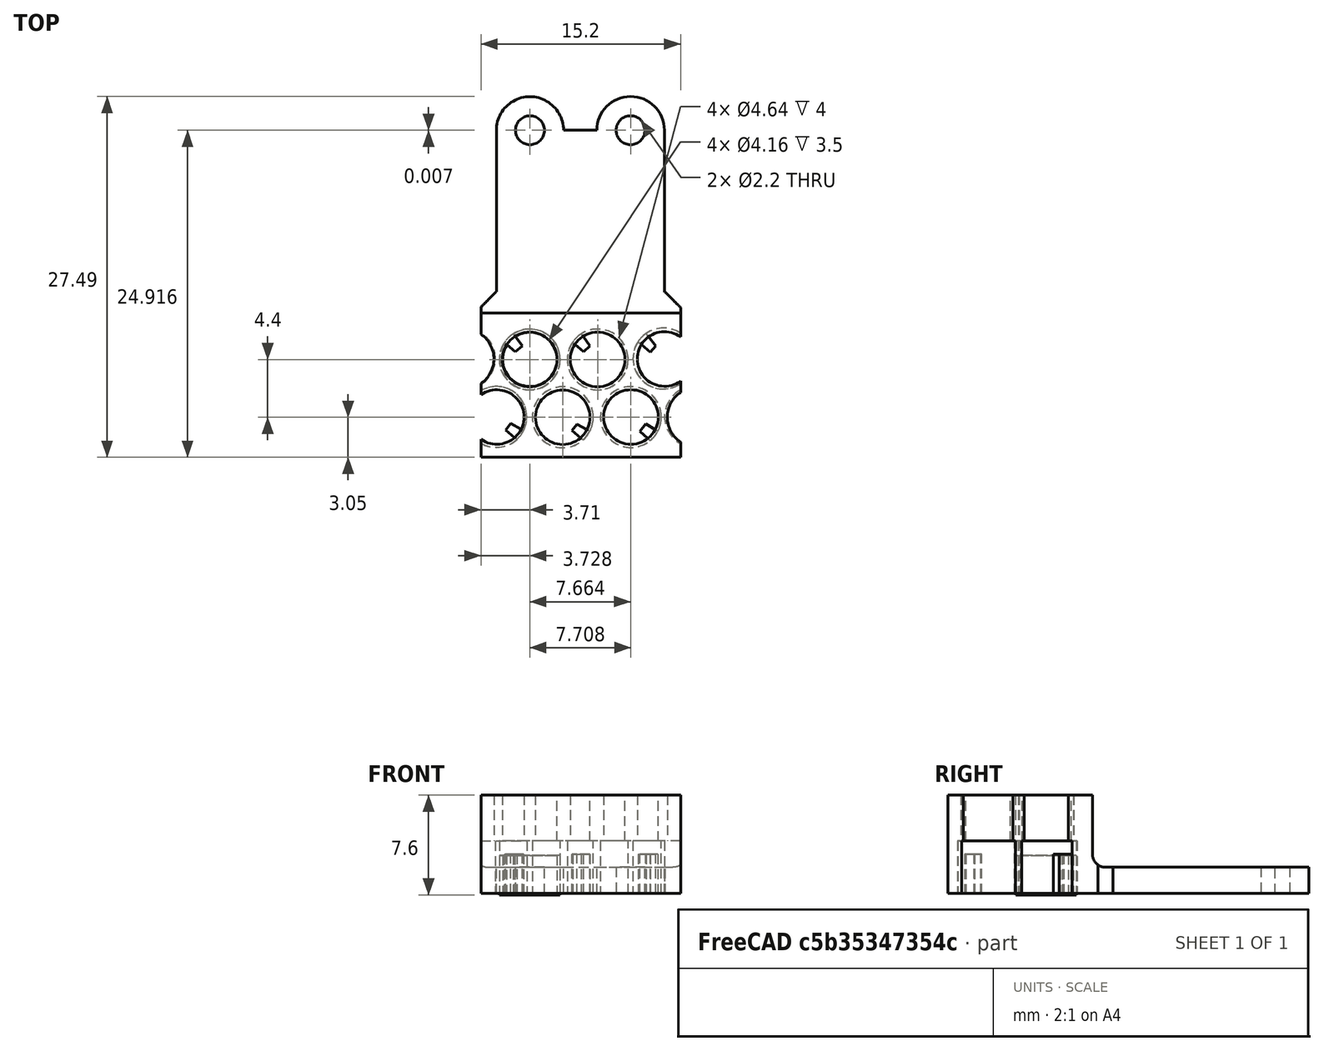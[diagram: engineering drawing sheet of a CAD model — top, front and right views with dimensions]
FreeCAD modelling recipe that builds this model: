
FCSTD DOCUMENT  (FreeCAD 0.16R6706 (Git))
Label: MotorHolder_1.1
License: All rights reserved
LicenseURL: http://en.wikipedia.org/wiki/All_rights_reserved
objects: Sketcher::SketchObject×4, PartDesign::Pad×4, Part::MultiFuse×2, Mesh::Feature×1, Part::Feature×1, PartDesign::Chamfer×1, Part::Box×1, Part::Cut×1, PartDesign::Fillet×1
note: 19 computed .brp shape members not serialized (recipe doc carries the construction recipe); baked Part::Feature solids carry a one-line shape summary decoded from their .brp

FEATURE [Mesh::Feature] Motor_Holder_2_1  label="Motor Holder 2.1"
FEATURE [Sketcher::SketchObject] Sketch
  Placement = pos=(0,0,-0.1) rot=(0,0,1;0rad)
  sketch-geometry (4):
    g0: LineSegment StartX=2.61412 StartY=9.20943 StartZ=0 EndX=2.48015 EndY=9.39721 EndZ=0
    g1: LineSegment StartX=1.96858 StartY=8.56337 StartZ=0 EndX=1.796 EndY=8.72024 EndZ=0
    g2: ArcOfCircle CenterX=3.71702 CenterY=7.46188 CenterZ=0 NormalX=0 NormalY=0 NormalZ=1 Radius=2.06647 StartAngle=2.57941 EndAngle=8.41696
    g3: ArcOfCircle CenterX=3.72 CenterY=7.46 CenterZ=0 NormalX=0 NormalY=0 NormalZ=1 Radius=2.3 StartAngle=2.5617 EndAngle=8.42331
  constraints (4):
    c: Coincident(g2,g0)
    c: Coincident(g2,g1)
    c: Coincident(g3,g0)
    c: Coincident(g3,g1)
FEATURE [Part::Feature] Solid
  shape: bbox 15.36 x 27.48 x 8.96 mm, 598 faces (baked)
FEATURE [PartDesign::Pad] Pad
  Length = 3
  Length2 = 100
  Placement = pos=(0,0,-0.1) rot=(0,0,1;0rad)
  Sketch = -> Sketch
  Type = 0
FEATURE [Sketcher::SketchObject] Sketch001
  sketch-geometry (24):
    g0: LineSegment StartX=1.16719 StartY=12.6074 StartZ=0 EndX=1.16719 EndY=24.9153 EndZ=0
    g1: LineSegment StartX=6.28798 StartY=24.9169 StartZ=0 EndX=8.82572 EndY=24.9169 EndZ=0
    g2: LineSegment StartX=13.9682 StartY=12.5724 StartZ=0 EndX=13.9682 EndY=24.9342 EndZ=0
    g3: ArcOfCircle CenterX=3.72758 CenterY=24.9165 CenterZ=0 NormalX=0 NormalY=0 NormalZ=1 Radius=2.56039 StartAngle=0.000160774 EndAngle=3.14208
    g4: ArcOfCircle CenterX=11.397 CenterY=24.9235 CenterZ=0 NormalX=0 NormalY=0 NormalZ=1 Radius=2.57125 StartAngle=0.00415218 EndAngle=3.14415
    g5: Circle CenterX=3.72758 CenterY=24.9165 CenterZ=0 NormalX=0 NormalY=0 NormalZ=1 Radius=1.1
    g6: Circle CenterX=11.392 CenterY=24.9235 CenterZ=0 NormalX=0 NormalY=0 NormalZ=1 Radius=1.1
    g7: LineSegment StartX=0 StartY=0 StartZ=0 EndX=15.2 EndY=0 EndZ=0
    g8: LineSegment StartX=15.2 StartY=12.5724 StartZ=0 EndX=13.9682 EndY=12.5724 EndZ=0
    g9: LineSegment StartX=0 StartY=12.6074 StartZ=0 EndX=1.16719 EndY=12.6074 EndZ=0
    g10: Circle CenterX=3.71 CenterY=7.45 CenterZ=0 NormalX=0 NormalY=0 NormalZ=1 Radius=2.32
    g11: Circle CenterX=8.8865 CenterY=7.45 CenterZ=0 NormalX=0 NormalY=0 NormalZ=1 Radius=2.32
    g12: Circle CenterX=11.4178 CenterY=3.06406 CenterZ=0 NormalX=0 NormalY=0 NormalZ=1 Radius=2.32
    g13: Circle CenterX=6.22788 CenterY=3.05007 CenterZ=0 NormalX=0 NormalY=0 NormalZ=1 Radius=2.32
    g14: ArcOfCircle CenterX=-1.2323 CenterY=7.51766 CenterZ=0 NormalX=0 NormalY=0 NormalZ=1 Radius=2.32 StartAngle=5.27236 EndAngle=7.29401
    g15: ArcOfCircle CenterX=1.16612 CenterY=3.07188 CenterZ=0 NormalX=0 NormalY=0 NormalZ=1 Radius=2.32 StartAngle=4.18574 EndAngle=8.38063
    g16: ArcOfCircle CenterX=13.8979 CenterY=7.52681 CenterZ=0 NormalX=0 NormalY=0 NormalZ=1 Radius=2.32 StartAngle=0.974907 EndAngle=5.30828
    g17: LineSegment StartX=15.2 StartY=9.44695 StartZ=0 EndX=15.2 EndY=12.5724 EndZ=0
    g18: LineSegment StartX=15.2 StartY=5.60666 StartZ=0 EndX=15.2 EndY=5.12562 EndZ=0
    g19: LineSegment StartX=15.2 StartY=1.04863 StartZ=0 EndX=15.2 EndY=0 EndZ=0
    g20: LineSegment StartX=0 StartY=0 StartZ=0 EndX=0 EndY=1.06625 EndZ=0
    g21: LineSegment StartX=0 StartY=5.07751 StartZ=0 EndX=0 EndY=5.55199 EndZ=0
    g22: LineSegment StartX=0 StartY=9.48333 StartZ=0 EndX=0 EndY=12.6074 EndZ=0
    g23: ArcOfCircle CenterX=16.3077 CenterY=3.08713 CenterZ=0 NormalX=0 NormalY=0 NormalZ=1 Radius=2.32 StartAngle=2.06854 EndAngle=4.21464
  constraints (50):
    c: Vertical(g0)
    c: Horizontal(g1)
    c: Vertical(g2)
    c: Coincident(g3,g0)
    c: Coincident(g3,g1)
    c: Coincident(g4,g1)
    c: Coincident(g4,g2)
    c: Coincident(g5,g3)
    c: Horizontal(g7)
    c: Coincident(g7,g-1)
    c: Coincident(g8,g2)
    c: Horizontal(g8)
    c: Coincident(g9,g0)
    c: Horizontal(g9)
    c: Radius(g10) = 2.32
    c: DistanceY(g-1,g10) = 7.45
    c: DistanceX(g-1,g10) = 3.71
    c: Radius(g11) = 2.32
    c: Radius(g12) = 2.32
    c: Radius(g13) = 2.32
    c: Radius(g15) = 2.32
    c: Radius(g16) = 2.32
    c: DistanceY(g-1,g11) = 7.45
    c: Coincident(g17,g16)
    c: Coincident(g17,g8)
    c: Vertical(g17)
    c: Coincident(g18,g16)
    c: Vertical(g18)
    c: Coincident(g19,g7)
    c: Vertical(g19)
    c: Coincident(g20,g-1)
    c: Coincident(g20,g15)
    c: Vertical(g20)
    c: Coincident(g21,g15)
    c: Coincident(g21,g14)
    c: Vertical(g21)
    c: Coincident(g22,g14)
    c: Coincident(g22,g9)
    c: Vertical(g22)
    c: DistanceX(g9,g8) = 15.2
    c: DistanceX(g14,g16) = 15.2
    c: DistanceX(g-1,g7) = 15.2
    c: Coincident(g23,g18)
    c: Coincident(g23,g19)
    c: DistanceX(g-1,g14) = 0
    c: DistanceX(g-1,g15) = 0
    c: Radius(g14) = 2.32
    c: Radius(g23) = 2.32
    c: Radius(g5) = 1.1
    c: Radius(g6) = 1.1
FEATURE [PartDesign::Pad] Pad001
  Length = 4
  Length2 = 100
  Sketch = -> Sketch001
  Type = 0
FEATURE [Sketcher::SketchObject] Sketch002
  Placement = pos=(0,0,4) rot=(0,0,1;0rad)
  sketch-geometry (16):
    g0: LineSegment StartX=0 StartY=0 StartZ=0 EndX=15.2 EndY=0 EndZ=0
    g1: Circle CenterX=3.71 CenterY=7.45 CenterZ=0 NormalX=0 NormalY=0 NormalZ=1 Radius=2.08
    g2: Circle CenterX=8.8865 CenterY=7.45 CenterZ=0 NormalX=0 NormalY=0 NormalZ=1 Radius=2.08
    g3: Circle CenterX=11.4178 CenterY=3.06406 CenterZ=0 NormalX=0 NormalY=0 NormalZ=1 Radius=2.08
    g4: Circle CenterX=6.22788 CenterY=3.05007 CenterZ=0 NormalX=0 NormalY=0 NormalZ=1 Radius=2.08
    g5: ArcOfCircle CenterX=-1.29213 CenterY=7.49891 CenterZ=0 NormalX=0 NormalY=0 NormalZ=1 Radius=2.27568 StartAngle=5.31622 EndAngle=7.25015
    g6: ArcOfCircle CenterX=1.20105 CenterY=3.06417 CenterZ=0 NormalX=0 NormalY=0 NormalZ=1 Radius=2.08 StartAngle=4.09681 EndAngle=8.46956
    g7: ArcOfCircle CenterX=13.9805 CenterY=7.48824 CenterZ=0 NormalX=0 NormalY=0 NormalZ=1 Radius=2.08 StartAngle=0.944332 EndAngle=5.33885
    g8: LineSegment StartX=15.2 StartY=5.80322 StartZ=0 EndX=15.2 EndY=4.94257 EndZ=0
    g9: LineSegment StartX=15.2 StartY=1.15374 StartZ=0 EndX=15.2 EndY=0 EndZ=0
    g10: LineSegment StartX=0 StartY=0 StartZ=0 EndX=0 EndY=1.36598 EndZ=0
    g11: LineSegment StartX=0 StartY=4.76237 StartZ=0 EndX=0 EndY=5.62564 EndZ=0
    g12: ArcOfCircle CenterX=16.4748 CenterY=3.04816 CenterZ=0 NormalX=0 NormalY=0 NormalZ=1 Radius=2.28338 StartAngle=2.1631 EndAngle=4.12008
    g13: LineSegment StartX=0 StartY=11 StartZ=0 EndX=15.2 EndY=11 EndZ=0
    g14: LineSegment StartX=15.2 StartY=9.17326 StartZ=0 EndX=15.2 EndY=11 EndZ=0
    g15: LineSegment StartX=0 StartY=9.37218 StartZ=0 EndX=0 EndY=11 EndZ=0
  constraints (36):
    c: Horizontal(g0)
    c: Coincident(g0,g-1)
    c: Radius(g1) = 2.08
    c: DistanceY(g-1,g1) = 7.45
    c: DistanceX(g-1,g1) = 3.71
    c: Radius(g2) = 2.08
    c: Radius(g3) = 2.08
    c: Radius(g4) = 2.08
    c: Radius(g6) = 2.08
    c: Radius(g7) = 2.08
    c: DistanceY(g-1,g2) = 7.45
    c: Coincident(g8,g7)
    c: Vertical(g8)
    c: Coincident(g9,g0)
    c: Vertical(g9)
    c: Coincident(g10,g-1)
    c: Coincident(g10,g6)
    c: Vertical(g10)
    c: Coincident(g11,g6)
    c: Coincident(g11,g5)
    c: Vertical(g11)
    c: DistanceX(g5,g7) = 15.2
    c: DistanceX(g-1,g0) = 15.2
    c: Coincident(g12,g8)
    c: Coincident(g12,g9)
    c: DistanceX(g-1,g5) = 0
    c: DistanceX(g-1,g6) = 0
    c: Horizontal(g13)
    c: Coincident(g14,g7)
    c: Coincident(g14,g13)
    c: Vertical(g14)
    c: DistanceY(g-1,g13) = 11
    c: DistanceX(g13,g-1) = 0
    c: Coincident(g15,g5)
    c: Coincident(g15,g13)
    c: DistanceX(g13,g13) = 15.2
FEATURE [PartDesign::Pad] Pad002
  Length = 3.5
  Length2 = 100
  Placement = pos=(0,0,4) rot=(0,0,1;0rad)
  Sketch = -> Sketch002
  Type = 0
FEATURE [Sketcher::SketchObject] Sketch003
  sketch-geometry (24):
    g0: LineSegment StartX=2.37867 StartY=9.53855 StartZ=0 EndX=3.14154 EndY=8.48461 EndZ=0
    g1: LineSegment StartX=3.14154 StartY=8.48461 StartZ=0 EndX=2.60525 EndY=8.03091 EndZ=0
    g2: LineSegment StartX=2.60525 StartY=8.03091 StartZ=0 EndX=1.60386 EndY=8.87946 EndZ=0
    g3: LineSegment StartX=2.37867 StartY=9.53855 StartZ=0 EndX=1.60386 EndY=8.87946 EndZ=0
    g4: LineSegment StartX=6.78436 StartY=8.94076 StartZ=0 EndX=7.81191 EndY=8.04644 EndZ=0
    g5: LineSegment StartX=7.81191 StartY=8.04644 StartZ=0 EndX=8.27871 EndY=8.4965 EndZ=0
    g6: LineSegment StartX=8.27871 StartY=8.4965 StartZ=0 EndX=7.51318 EndY=9.56846 EndZ=0
    g7: LineSegment StartX=7.51318 StartY=9.56846 StartZ=0 EndX=6.78436 EndY=8.94076 EndZ=0
    g8: LineSegment StartX=11.6397 StartY=9.07747 StartZ=0 EndX=12.905 EndY=8.01886 EndZ=0
    g9: LineSegment StartX=12.905 StartY=8.01886 StartZ=0 EndX=13.2996 EndY=8.47427 EndZ=0
    g10: LineSegment StartX=13.2996 StartY=8.47427 StartZ=0 EndX=12.401 EndY=9.69575 EndZ=0
    g11: LineSegment StartX=12.401 StartY=9.69575 StartZ=0 EndX=11.6397 EndY=9.07747 EndZ=0
    g12: LineSegment StartX=12.1046 StartY=1.97636 StartZ=0 EndX=13.3056 EndY=0.90266 EndZ=0
    g13: LineSegment StartX=13.3056 StartY=0.90266 StartZ=0 EndX=13.8986 EndY=1.72895 EndZ=0
    g14: LineSegment StartX=13.8986 StartY=1.72895 StartZ=0 EndX=12.5452 EndY=2.53763 EndZ=0
    g15: LineSegment StartX=12.5452 StartY=2.53763 StartZ=0 EndX=12.1046 EndY=1.97636 EndZ=0
    g16: LineSegment StartX=8.70009 StartY=1.7485 StartZ=0 EndX=7.31743 EndY=2.50872 EndZ=0
    g17: LineSegment StartX=7.31743 StartY=2.50872 StartZ=0 EndX=6.93042 EndY=2.02516 EndZ=0
    g18: LineSegment StartX=6.93042 StartY=2.02516 StartZ=0 EndX=8.13703 EndY=1.0298 EndZ=0
    g19: LineSegment StartX=8.13703 StartY=1.0298 StartZ=0 EndX=8.70009 EndY=1.7485 EndZ=0
    g20: LineSegment StartX=2.27306 StartY=2.56746 StartZ=0 EndX=3.50885 EndY=1.8824 EndZ=0
    g21: LineSegment StartX=3.50885 StartY=1.8824 StartZ=0 EndX=2.89778 EndY=1.21181 EndZ=0
    g22: LineSegment StartX=2.89778 StartY=1.21181 StartZ=0 EndX=1.89388 EndY=2.05588 EndZ=0
    g23: LineSegment StartX=1.89388 StartY=2.05588 StartZ=0 EndX=2.27306 EndY=2.56746 EndZ=0
  constraints (24):
    c: Coincident(g1,g0)
    c: Coincident(g2,g1)
    c: Coincident(g3,g0)
    c: Coincident(g3,g2)
    c: Coincident(g4,g5)
    c: Coincident(g5,g6)
    c: Coincident(g6,g7)
    c: Coincident(g7,g4)
    c: Coincident(g8,g9)
    c: Coincident(g9,g10)
    c: Coincident(g10,g11)
    c: Coincident(g11,g8)
    c: Coincident(g12,g13)
    c: Coincident(g13,g14)
    c: Coincident(g14,g15)
    c: Coincident(g15,g12)
    c: Coincident(g16,g17)
    c: Coincident(g17,g18)
    c: Coincident(g18,g19)
    c: Coincident(g19,g16)
    c: Coincident(g20,g21)
    c: Coincident(g21,g22)
    c: Coincident(g22,g23)
    c: Coincident(g23,g20)
FEATURE [PartDesign::Pad] Pad003
  Length = 3
  Length2 = 100
  Sketch = -> Sketch003
  Type = 0
FEATURE [PartDesign::Chamfer] Chamfer
  Base = -> Pad001 [Edge14,Edge35]
  Size = 1.16
FEATURE [Part::MultiFuse] Fusion
  Shapes = -> [Chamfer,Pad003,Pad002]
FEATURE [Part::Box] Box  label="Würfel"
  Height = 10
  Length = 15.2
  Placement = pos=(0,11,2) rot=(0,0,1;0rad)
  Width = 18
FEATURE [Part::Cut] Cut
  Base = -> Fusion
  Tool = -> Box
FEATURE [PartDesign::Fillet] Fillet
  Base = -> Cut [Edge80]
  Radius = 1
FEATURE [Part::MultiFuse] Fusion001  label="MotorHolder"
  Shapes = -> [Fillet,Cut]
